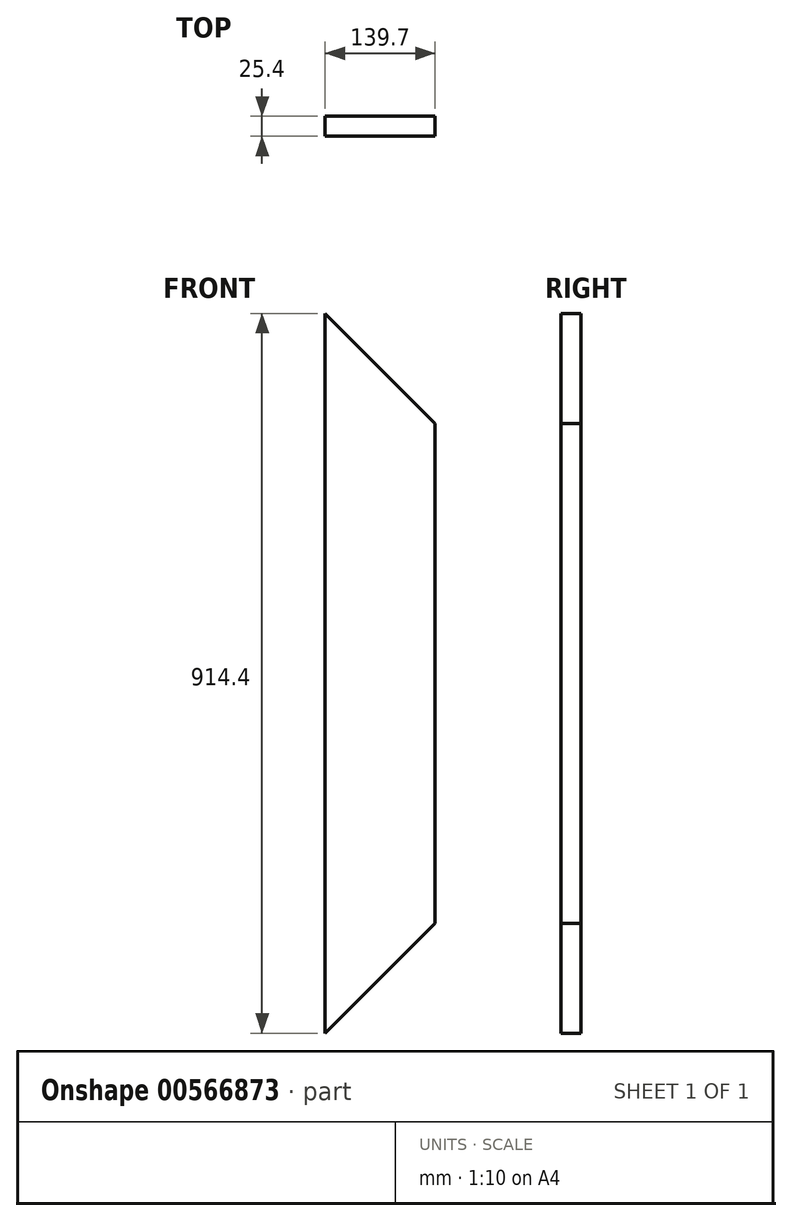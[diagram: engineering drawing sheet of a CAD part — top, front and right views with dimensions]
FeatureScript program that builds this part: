
annotation { "Feature Type Name" : "Feature", "Feature Type Description" : "" }
export const myFeature = defineFeature(function(context is Context, id is Id, definition is map)
    precondition{}
    {
        {
            var Q0;
            Q0=qCreatedBy(makeId("Front.planeOp"),FACE);
            var sketch = newSketch(context, id + "F0", { "sketchPlane" : qUnion([Q0])});
            skLineSegment(sketch, "E0", {"start": v(0, 457.2) * mm, "end": v(0, -457.2) * mm});
            skLineSegment(sketch, "E1", {"start": v(0, -457.2) * mm, "end": v(139.7, -317.5) * mm});
            skLineSegment(sketch, "E2", {"start": v(139.7, -317.5) * mm, "end": v(139.7, 317.5) * mm});
            skLineSegment(sketch, "E3", {"start": v(139.7, 317.5) * mm, "end": v(0, 457.2) * mm});
            skPoint(sketch, "E4", {"position": v(0, 0) * mm});
            skSolve(sketch);
        }
        {
            var Q0;
            Q0=makeQuery(id+"F0.imprint","IMPRINT",FACE,{"disambiguationData":[TD([[makeQuery(id+"F0.imprint","IMPRINT",EDGE,{"derivedFrom":sQuery(id+"F0.wireOp",EDGE,"E0")}),1.0]])]});
            extrude(context, id + "F1", {"entities" : qUnion([Q0]), "depth" : 25.4 * mm, "offsetDistance" : 25.4 * mm});
        }
    });
